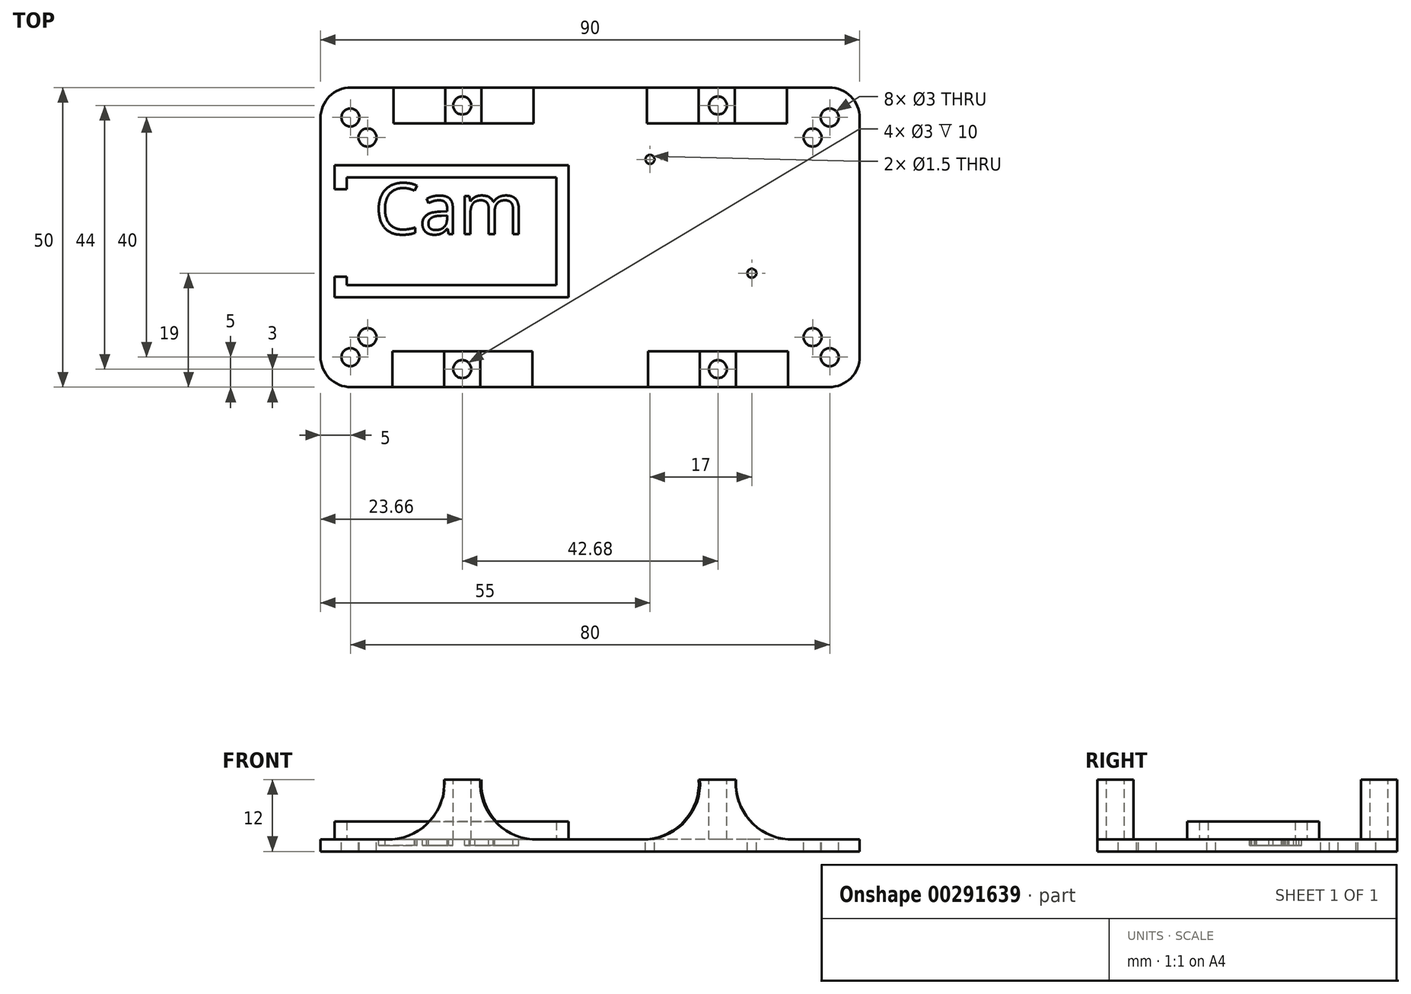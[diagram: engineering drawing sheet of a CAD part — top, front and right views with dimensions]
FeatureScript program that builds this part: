
annotation { "Feature Type Name" : "Feature", "Feature Type Description" : "" }
export const myFeature = defineFeature(function(context is Context, id is Id, definition is map)
    precondition{}
    {
        {
            var Q0;
            Q0=qCreatedBy(makeId("Top.planeOp"),FACE);
            var sketch = newSketch(context, id + "F0", { "sketchPlane" : qUnion([Q0])});
            skLineSegment(sketch, "E0.bottom", {"start": v(0, 0) * mm, "end": v(90, 0) * mm});
            skLineSegment(sketch, "E0.top", {"start": v(0, 50) * mm, "end": v(90, 50) * mm});
            skLineSegment(sketch, "E0.left", {"start": v(0, 0) * mm, "end": v(0, 50) * mm});
            skLineSegment(sketch, "E0.right", {"start": v(90, 0) * mm, "end": v(90, 50) * mm});
            skSolve(sketch);
        }
        {
            var Q0;
            Q0=qSketchRegion(id+"F0",true);
            extrude(context, id + "F1", {"entities" : qUnion([Q0]), "depth" : 2 * mm, "offsetDistance" : 25.4 * mm});
        }
        {
            var Q0;
            Q0=makeQuery(id+"F1.opExtrude","CAP_FACE",FACE,{"disambiguationData":[OSD([sQuery(id+"F0.wireOp",EDGE,"E0.bottom"),sQuery(id+"F0.wireOp",EDGE,"E0.top"),sQuery(id+"F0.wireOp",EDGE,"E0.left"),sQuery(id+"F0.wireOp",EDGE,"E0.right")])],"isStart":false});
            cPlane(context, id + "F2", {"entities" : qUnion([Q0]), "cplaneType" : CPlaneType.OFFSET, "offset" : 0 * mm, "width" : 152.4 * mm, "height" : 152.4 * mm});
        }
        {
            var Q0;
            Q0=makeQuery(id+"F1.opExtrude","SWEPT_EDGE",EDGE,{"disambiguationData":[OSD([sQuery(id+"F0.wireOp",EDGE,"E0.bottom"),sQuery(id+"F0.wireOp",EDGE,"E0.right")])]});
            fillet(context, id + "F3", {"entities" : qUnion([Q0]), "radius" : 5.08 * mm, "tangentPropagation" : true, "allowEdgeOverflow" : false});
        }
        {
            var Q0;
            Q0=makeQuery(id+"F1.opExtrude","SWEPT_EDGE",EDGE,{"disambiguationData":[OSD([sQuery(id+"F0.wireOp",EDGE,"E0.top"),sQuery(id+"F0.wireOp",EDGE,"E0.right")])]});
            fillet(context, id + "F4", {"entities" : qUnion([Q0]), "radius" : 5.08 * mm, "tangentPropagation" : true, "allowEdgeOverflow" : false});
        }
        {
            var Q0;
            Q0=makeQuery(id+"F1.opExtrude","SWEPT_EDGE",EDGE,{"disambiguationData":[OSD([sQuery(id+"F0.wireOp",EDGE,"E0.top"),sQuery(id+"F0.wireOp",EDGE,"E0.left")])]});
            fillet(context, id + "F5", {"entities" : qUnion([Q0]), "radius" : 5.08 * mm, "tangentPropagation" : true, "allowEdgeOverflow" : false});
        }
        {
            var Q0;
            Q0=makeQuery(id+"F1.opExtrude","SWEPT_EDGE",EDGE,{"disambiguationData":[OSD([sQuery(id+"F0.wireOp",EDGE,"E0.bottom"),sQuery(id+"F0.wireOp",EDGE,"E0.left")])]});
            fillet(context, id + "F6", {"entities" : qUnion([Q0]), "radius" : 5.08 * mm, "tangentPropagation" : true, "allowEdgeOverflow" : false});
        }
        {
            var Q0;
            Q0=qCreatedBy(id+"F2.planeOp",FACE);
            var sketch = newSketch(context, id + "F7", { "sketchPlane" : qUnion([Q0])});
            skLineSegment(sketch, "E1", {"start": v(45, 0) * mm, "end": v(45, 70.78) * mm});
            skLineSegment(sketch, "E2", {"start": v(0, 25) * mm, "end": v(105.16, 25) * mm});
            skSolve(sketch);
        }
        {
            var Q0;
            Q0=qCreatedBy(id+"F2.planeOp",FACE);
            var sketch = newSketch(context, id + "F8", { "sketchPlane" : qUnion([Q0])});
            skCircle(sketch, "E3", {"center": v(85, 5) * mm, "radius": 1.5 * mm});
            skCircle(sketch, "E4", {"center": v(82.15, 8.34) * mm, "radius": 1.5 * mm});
            skCircle(sketch, "E5.MirrorC", {"center": v(82.15, 41.66) * mm, "radius": 1.5 * mm});
            skCircle(sketch, "E6.MirrorC", {"center": v(85, 45) * mm, "radius": 1.5 * mm});
            skCircle(sketch, "E7.MirrorC", {"center": v(7.85, 41.66) * mm, "radius": 1.5 * mm});
            skCircle(sketch, "E8.MirrorC", {"center": v(5, 45) * mm, "radius": 1.5 * mm});
            skCircle(sketch, "E9.MirrorC", {"center": v(7.85, 8.34) * mm, "radius": 1.5 * mm});
            skCircle(sketch, "E10.MirrorC", {"center": v(5, 5) * mm, "radius": 1.5 * mm});
            skSolve(sketch);
        }
        {
            var Q0;
            Q0=qSketchRegion(id+"F8",true);
            extrude(context, id + "F9", {"entities" : qUnion([Q0]), "operationType" : NewBodyOperationType.REMOVE, "oppositeDirection" : true, "depth" : 25.4 * mm});
        }
        {
            var Q0;
            Q0=qCreatedBy(id+"F2.planeOp",FACE);
            var sketch = newSketch(context, id + "F10", { "sketchPlane" : qUnion([Q0])});
            skLineSegment(sketch, "E11.bottom", {"start": v(60, 44) * mm, "end": v(80, 44) * mm});
            skLineSegment(sketch, "E11.top", {"start": v(60, 15) * mm, "end": v(80, 15) * mm});
            skLineSegment(sketch, "E11.left", {"start": v(60, 44) * mm, "end": v(60, 15) * mm});
            skLineSegment(sketch, "E11.right", {"start": v(80, 44) * mm, "end": v(80, 15) * mm});
            skCircle(sketch, "E12", {"center": v(55, 38) * mm, "radius": 0.75 * mm});
            skCircle(sketch, "E13", {"center": v(72, 19) * mm, "radius": 0.75 * mm});
            skSolve(sketch);
        }
        {
            var Q0;
            Q0=makeQuery(id+"F10.imprint","IMPRINT",FACE,{"disambiguationData":[TD([[makeQuery(id+"F10.imprint","IMPRINT",EDGE,{"derivedFrom":sQuery(id+"F10.wireOp",EDGE,"E13")}),1.0]])]});
            var Q1;
            Q1=makeQuery(id+"F10.imprint","IMPRINT",FACE,{"disambiguationData":[TD([[makeQuery(id+"F10.imprint","IMPRINT",EDGE,{"derivedFrom":sQuery(id+"F10.wireOp",EDGE,"E12")}),1.0]])]});
            extrude(context, id + "F11", {"entities" : qUnion([Q0, Q1]), "operationType" : NewBodyOperationType.REMOVE, "oppositeDirection" : true, "depth" : 25.4 * mm});
        }
        {
            var Q0;
            Q0=qCreatedBy(id+"F2.planeOp",FACE);
            var sketch = newSketch(context, id + "F12", { "sketchPlane" : qUnion([Q0])});
            skLineSegment(sketch, "E14.bottom", {"start": v(4, 39) * mm, "end": v(39, 39) * mm});
            skLineSegment(sketch, "E14.top", {"start": v(4, 21) * mm, "end": v(39, 21) * mm});
            skLineSegment(sketch, "E14.right", {"start": v(39, 39) * mm, "end": v(39, 21) * mm});
            skText(sketch, "E15", { "text": "Cam", "fontName": "OpenSans-Regular.ttf"});
            skLineSegment(sketch, "E16", {"start": v(4, 37) * mm, "end": v(2, 37) * mm});
            skLineSegment(sketch, "E17", {"start": v(2, 37) * mm, "end": v(2, 41) * mm});
            skLineSegment(sketch, "E18", {"start": v(2, 41) * mm, "end": v(41, 41) * mm});
            skLineSegment(sketch, "E19", {"start": v(41, 41) * mm, "end": v(41, 19) * mm});
            skLineSegment(sketch, "E20", {"start": v(41, 19) * mm, "end": v(2, 19) * mm});
            skLineSegment(sketch, "E21", {"start": v(2, 19) * mm, "end": v(2, 22.44) * mm});
            skLineSegment(sketch, "E22", {"start": v(2, 22.44) * mm, "end": v(4, 22.44) * mm});
            skLineSegment(sketch, "E23", {"start": v(4, 22.44) * mm, "end": v(4, 21) * mm});
            skLineSegment(sketch, "E24", {"start": v(4, 37) * mm, "end": v(4, 39) * mm});
            const initialGuessF12  = {"E15": [0.009, 0.02554, 1, 0, 0.00852]};
            skSetInitialGuess(sketch, initialGuessF12);
            skSolve(sketch);
        }
        {
            var Q0;
            Q0=makeQuery(id+"F12.imprint","IMPRINT",FACE,{"disambiguationData":[TD([[makeQuery(id+"F12.imprint","IMPRINT",EDGE,{"derivedFrom":sQuery(id+"F12.wireOp",EDGE,"E15.sketch_text.stroke-0")}),-1.0]])]});
            var Q1;
            Q1=makeQuery(id+"F12.imprint","IMPRINT",FACE,{"disambiguationData":[TD([[makeQuery(id+"F12.imprint","IMPRINT",EDGE,{"derivedFrom":sQuery(id+"F12.wireOp",EDGE,"E15.sketch_text.stroke-15")}),-1.0]])]});
            var Q2;
            Q2=makeQuery(id+"F12.imprint","IMPRINT",FACE,{"disambiguationData":[TD([[makeQuery(id+"F12.imprint","IMPRINT",EDGE,{"derivedFrom":sQuery(id+"F12.wireOp",EDGE,"E15.sketch_text.stroke-42")}),-1.0]])]});
            extrude(context, id + "F13", {"entities" : qUnion([Q0, Q1, Q2]), "operationType" : NewBodyOperationType.REMOVE, "oppositeDirection" : true, "depth" : 1 * mm, "offsetDistance" : 25.4 * mm});
        }
        {
            var Q0;
            Q0=qCreatedBy(id+"F2.planeOp",FACE);
            var sketch = newSketch(context, id + "F14", { "sketchPlane" : qUnion([Q0])});
            skLineSegment(sketch, "E25.bottom", {"start": v(4.38, 35) * mm, "end": v(39.38, 35) * mm});
            skLineSegment(sketch, "E25.top", {"start": v(4.38, 17) * mm, "end": v(39.38, 17) * mm});
            skLineSegment(sketch, "E25.right", {"start": v(39.38, 35) * mm, "end": v(39.38, 17) * mm});
            skLineSegment(sketch, "E26", {"start": v(4.38, 33) * mm, "end": v(2.38, 33) * mm});
            skLineSegment(sketch, "E27", {"start": v(2.38, 33) * mm, "end": v(2.38, 37) * mm});
            skLineSegment(sketch, "E28", {"start": v(2.38, 37) * mm, "end": v(41.38, 37) * mm});
            skLineSegment(sketch, "E29", {"start": v(41.38, 37) * mm, "end": v(41.38, 15) * mm});
            skLineSegment(sketch, "E30", {"start": v(41.38, 15) * mm, "end": v(2.38, 15) * mm});
            skLineSegment(sketch, "E31", {"start": v(2.38, 15) * mm, "end": v(2.38, 18.44) * mm});
            skLineSegment(sketch, "E32", {"start": v(2.38, 18.44) * mm, "end": v(4.38, 18.44) * mm});
            skLineSegment(sketch, "E33", {"start": v(4.38, 18.44) * mm, "end": v(4.38, 17) * mm});
            skLineSegment(sketch, "E34", {"start": v(4.38, 33) * mm, "end": v(4.38, 35) * mm});
            skSolve(sketch);
        }
        {
            var Q0;
            Q0 = qSketchRegion(id + "F14", true);
            extrude(context, id + "F15", {"entities" : qUnion([Q0]), "operationType" : NewBodyOperationType.ADD, "depth" : 3 * mm, "offsetDistance" : 25.4 * mm});
        }
        {
            var Q0;
            Q0=makeQuery(id+"F1.opExtrude","SWEPT_FACE",FACE,{"disambiguationData":[OSD([sQuery(id+"F0.wireOp",EDGE,"E0.bottom")])]});
            cPlane(context, id + "F16", {"entities" : qUnion([Q0]), "cplaneType" : CPlaneType.OFFSET, "offset" : 0 * mm, "width" : 152.4 * mm, "height" : 152.4 * mm});
        }
        {
            var Q0;
            Q0=qCreatedBy(id+"F16.planeOp",FACE);
            var sketch = newSketch(context, id + "F17", { "sketchPlane" : qUnion([Q0])});
            skArc(sketch, "E35", {"start": v(10.52, 2) * mm, "mid": v(17.87, 4.69) * mm, "end": v(20.66, 12) * mm});
            skLineSegment(sketch, "E36", {"start": v(23.66, 0) * mm, "end": v(23.66, 15.24) * mm});
            skLineSegment(sketch, "E37", {"start": v(20.66, 12) * mm, "end": v(20.66, 12) * mm});
            skLineSegment(sketch, "E38.MirrorCS", {"start": v(26.66, 12) * mm, "end": v(26.66, 12) * mm});
            skArc(sketch, "E39.MirrorCS", {"start": v(36.8, 2) * mm, "mid": v(29.45, 4.69) * mm, "end": v(26.66, 12) * mm});
            skLineSegment(sketch, "E40", {"start": v(20.66, 12) * mm, "end": v(26.66, 12) * mm});
            skLineSegment(sketch, "E41", {"start": v(10.52, 2) * mm, "end": v(36.8, 2) * mm});
            skLineSegment(sketch, "E42", {"start": v(45, 0) * mm, "end": v(45, 41.84) * mm});
            skLineSegment(sketch, "E43.MirrorCS", {"start": v(63.34, 12) * mm, "end": v(63.34, 12) * mm});
            skArc(sketch, "E44.MirrorCS", {"start": v(53.2, 2) * mm, "mid": v(60.55, 4.69) * mm, "end": v(63.34, 12) * mm});
            skArc(sketch, "E45.MirrorCS", {"start": v(79.48, 2) * mm, "mid": v(72.13, 4.69) * mm, "end": v(69.34, 12) * mm});
            skLineSegment(sketch, "E46.MirrorCS", {"start": v(69.34, 12) * mm, "end": v(69.34, 12) * mm});
            skLineSegment(sketch, "E47.MirrorCS", {"start": v(69.34, 12) * mm, "end": v(63.34, 12) * mm});
            skLineSegment(sketch, "E48.MirrorCS", {"start": v(79.48, 2) * mm, "end": v(53.2, 2) * mm});
            skSolve(sketch);
        }
        {
            var Q0;
            Q0 = qSketchRegion(id + "F17", true);
            extrude(context, id + "F18", {"entities" : qUnion([Q0]), "operationType" : NewBodyOperationType.ADD, "oppositeDirection" : true, "depth" : 6 * mm});
        }
        {
            var Q0;
            Q0=makeQuery(id+"F1.opExtrude","SWEPT_FACE",FACE,{"disambiguationData":[OSD([sQuery(id+"F0.wireOp",EDGE,"E0.top")])]});
            cPlane(context, id + "F19", {"entities" : qUnion([Q0]), "cplaneType" : CPlaneType.OFFSET, "offset" : 0 * mm, "width" : 152.4 * mm, "height" : 152.4 * mm});
        }
        {
            var Q0;
            Q0=makeQuery(id+"F18.opExtrude","SWEPT_FACE",FACE,{"disambiguationData":[OSD([sQuery(id+"F17.wireOp",EDGE,"E40")])]});
            cPlane(context, id + "F20", {"entities" : qUnion([Q0]), "cplaneType" : CPlaneType.OFFSET, "offset" : 0 * mm, "width" : 152.4 * mm, "height" : 152.4 * mm});
        }
        {
            var Q0;
            Q0=qCreatedBy(id+"F19.planeOp",FACE);
            var sketch = newSketch(context, id + "F21", { "sketchPlane" : qUnion([Q0])});
            skArc(sketch, "E49", {"start": v(-79.29, 2) * mm, "mid": v(-71.94, 4.69) * mm, "end": v(-69.14, 12) * mm});
            skLineSegment(sketch, "E50", {"start": v(-66.14, 0) * mm, "end": v(-66.14, 16.24) * mm});
            skLineSegment(sketch, "E51", {"start": v(-69.14, 12) * mm, "end": v(-69.14, 12) * mm});
            skLineSegment(sketch, "E52.MirrorCS", {"start": v(-63.14, 12) * mm, "end": v(-63.14, 12) * mm});
            skArc(sketch, "E53.MirrorCS", {"start": v(-53, 2) * mm, "mid": v(-60.35, 4.69) * mm, "end": v(-63.14, 12) * mm});
            skLineSegment(sketch, "E54", {"start": v(-69.14, 12) * mm, "end": v(-63.14, 12) * mm});
            skLineSegment(sketch, "E55", {"start": v(-79.29, 2) * mm, "end": v(-53, 2) * mm});
            skLineSegment(sketch, "E56", {"start": v(-45, -11.35) * mm, "end": v(-45, 30.48) * mm});
            skLineSegment(sketch, "E57.MirrorCS", {"start": v(-26.86, 12) * mm, "end": v(-26.86, 12) * mm});
            skArc(sketch, "E58.MirrorCS", {"start": v(-37, 2) * mm, "mid": v(-29.65, 4.69) * mm, "end": v(-26.86, 12) * mm});
            skArc(sketch, "E59.MirrorCS", {"start": v(-10.71, 2) * mm, "mid": v(-18.06, 4.69) * mm, "end": v(-20.86, 12) * mm});
            skLineSegment(sketch, "E60.MirrorCS", {"start": v(-20.86, 12) * mm, "end": v(-20.86, 12) * mm});
            skLineSegment(sketch, "E61.MirrorCS", {"start": v(-20.86, 12) * mm, "end": v(-26.86, 12) * mm});
            skLineSegment(sketch, "E62.MirrorCS", {"start": v(-10.71, 2) * mm, "end": v(-37, 2) * mm});
            skSolve(sketch);
        }
        {
            var Q0;
            Q0 = qSketchRegion(id + "F21", true);
            extrude(context, id + "F22", {"entities" : qUnion([Q0]), "operationType" : NewBodyOperationType.ADD, "oppositeDirection" : true, "depth" : 6 * mm});
        }
        {
            var Q0;
            Q0=qCreatedBy(id+"F20.planeOp",FACE);
            var sketch = newSketch(context, id + "F23", { "sketchPlane" : qUnion([Q0])});
            skCircle(sketch, "E63", {"center": v(23.66, 3) * mm, "radius": 1.5 * mm});
            skCircle(sketch, "E64.MirrorC", {"center": v(66.34, 3) * mm, "radius": 1.5 * mm});
            skCircle(sketch, "E65.MirrorC", {"center": v(23.66, 47) * mm, "radius": 1.5 * mm});
            skCircle(sketch, "E66.MirrorC", {"center": v(66.34, 47) * mm, "radius": 1.5 * mm});
            skSolve(sketch);
        }
        {
            var Q0;
            Q0 = qSketchRegion(id + "F23", true);
            extrude(context, id + "F24", {"entities" : qUnion([Q0]), "operationType" : NewBodyOperationType.REMOVE, "oppositeDirection" : true, "depth" : 10 * mm});
        }
    });
